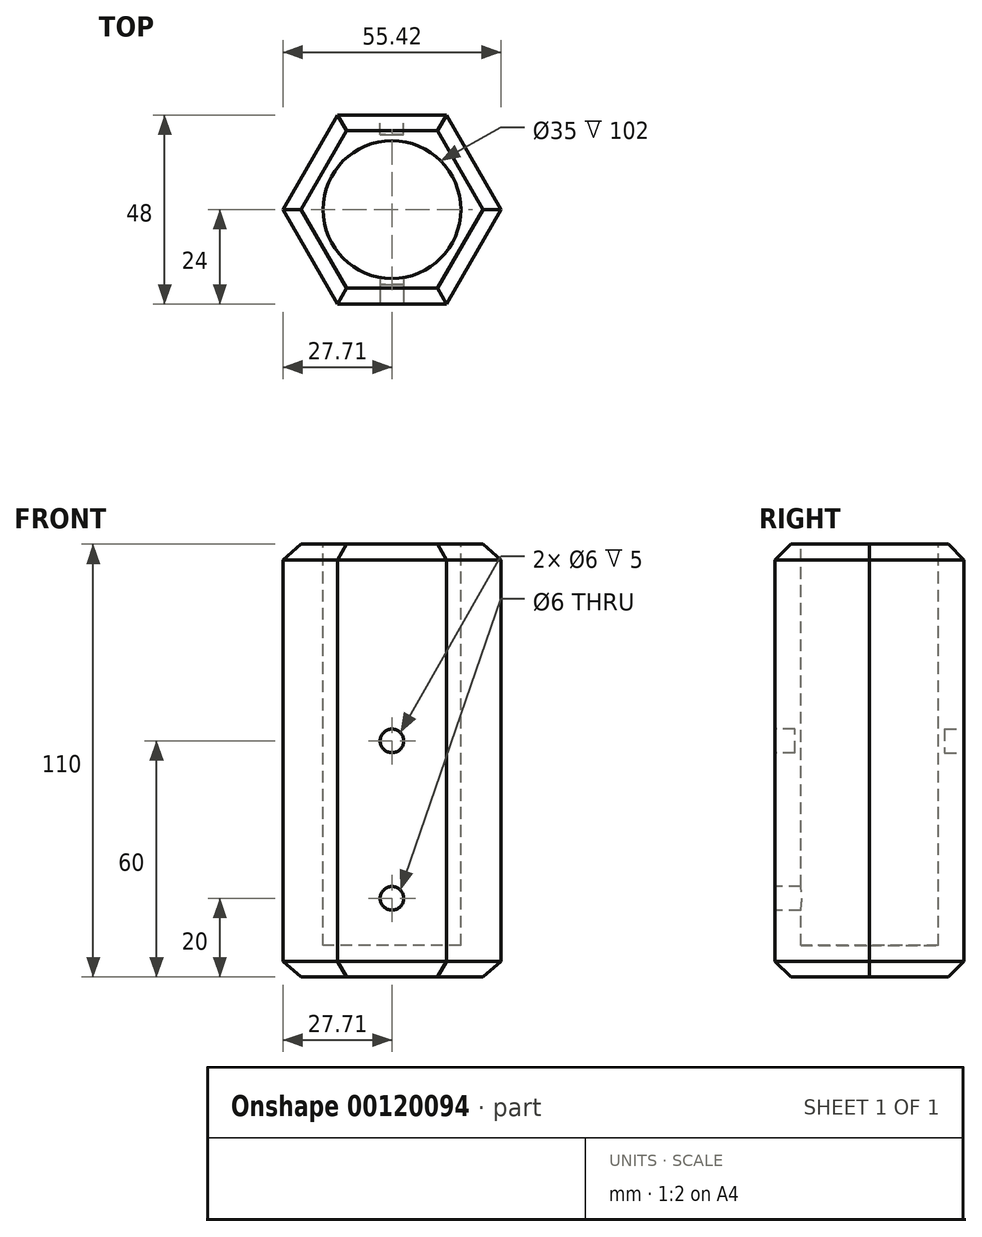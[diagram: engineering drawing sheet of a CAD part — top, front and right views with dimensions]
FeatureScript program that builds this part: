
annotation { "Feature Type Name" : "Feature", "Feature Type Description" : "" }
export const myFeature = defineFeature(function(context is Context, id is Id, definition is map)
    precondition{}
    {
        {
            var Q0;
            Q0=qCreatedBy(makeId("Top.planeOp"),FACE);
            var sketch = newSketch(context, id + "F0", { "sketchPlane" : qUnion([Q0])});
            skCircle(sketch, "E0.cCircle", {"center": v(0, 0) * mm, "radius": 24 * mm, "construction": true});
            skLineSegment(sketch, "E0.0", {"start": v(13.86, -24) * mm, "end": v(-13.86, -24) * mm});
            skLineSegment(sketch, "E0.1", {"start": v(-13.86, -24) * mm, "end": v(-27.71, 0) * mm});
            skLineSegment(sketch, "E0.2", {"start": v(-27.71, 0) * mm, "end": v(-13.86, 24) * mm});
            skLineSegment(sketch, "E0.3", {"start": v(-13.86, 24) * mm, "end": v(13.86, 24) * mm});
            skLineSegment(sketch, "E0.4", {"start": v(13.86, 24) * mm, "end": v(27.71, 0) * mm});
            skLineSegment(sketch, "E0.5", {"start": v(27.71, 0) * mm, "end": v(13.86, -24) * mm});
            skPoint(sketch, "E0.0.midPoint", {"position": v(0, -24) * mm});
            skSolve(sketch);
        }
        {
            var Q0;
            Q0 = qSketchRegion(id + "F0", true);
            extrude(context, id + "F1", {"entities" : qUnion([Q0]), "endBound" : BoundingType.SYMMETRIC, "depth" : 110 * mm});
        }
        {
            var Q0;
            Q0=makeQuery(id+"F1.opExtrude","CAP_FACE",FACE,{"disambiguationData":[OSD([sQuery(id+"F0.wireOp",EDGE,"E0.0"),sQuery(id+"F0.wireOp",EDGE,"E0.1"),sQuery(id+"F0.wireOp",EDGE,"E0.2"),sQuery(id+"F0.wireOp",EDGE,"E0.3"),sQuery(id+"F0.wireOp",EDGE,"E0.4"),sQuery(id+"F0.wireOp",EDGE,"E0.5")])],"isStart":false});
            var sketch = newSketch(context, id + "F2", { "sketchPlane" : qUnion([Q0])});
            skCircle(sketch, "E1", {"center": v(0, 0) * mm, "radius": 17.5 * mm});
            skSolve(sketch);
        }
        {
            var Q0;
            Q0 = qSketchRegion(id + "F2", true);
            extrude(context, id + "F3", {"entities" : qUnion([Q0]), "operationType" : NewBodyOperationType.REMOVE, "oppositeDirection" : true, "depth" : 102 * mm});
        }
        {
            var Q0;
            Q0=makeQuery(id+"F1.opExtrude","SWEPT_FACE",FACE,{"disambiguationData":[OSD([sQuery(id+"F0.wireOp",EDGE,"E0.0")])]});
            var sketch = newSketch(context, id + "F4", { "sketchPlane" : qUnion([Q0])});
            skLineSegment(sketch, "E2", {"start": v(0, -55) * mm, "end": v(0, 5) * mm});
            skPoint(sketch, "E2.endSnap0", {"position": v(0, -55) * mm});
            skCircle(sketch, "E3", {"center": v(0, 5) * mm, "radius": 3 * mm});
            skSolve(sketch);
        }
        {
            var Q0;
            Q0 = qSketchRegion(id + "F4", true);
            extrude(context, id + "F5", {"entities" : qUnion([Q0]), "operationType" : NewBodyOperationType.REMOVE, "oppositeDirection" : true, "depth" : 5 * mm});
        }
        {
            var Q0;
            Q0=makeQuery(id+"F1.opExtrude","SWEPT_FACE",FACE,{"disambiguationData":[OSD([sQuery(id+"F0.wireOp",EDGE,"E0.0")])]});
            var sketch = newSketch(context, id + "F6", { "sketchPlane" : qUnion([Q0])});
            skLineSegment(sketch, "E4", {"start": v(0, 5) * mm, "end": v(0, -35) * mm});
            skCircle(sketch, "E5", {"center": v(0, -35) * mm, "radius": 0.5 * mm});
            skCircle(sketch, "E6", {"center": v(0, -35) * mm, "radius": 3 * mm});
            skSolve(sketch);
        }
        {
            var Q0;
            Q0 = qSketchRegion(id + "F6", true);
            var Q1;
            Q1=makeQuery(id+"F6.imprint","IMPRINT",FACE,{"disambiguationData":[TD([[makeQuery(id+"F6.imprint","IMPRINT",EDGE,{"derivedFrom":sQuery(id+"F6.wireOp",EDGE,"E5")}),1.0]])]});
            extrude(context, id + "F7", {"entities" : qUnion([Q0, Q1]), "operationType" : NewBodyOperationType.REMOVE, "oppositeDirection" : true, "depth" : 25 * mm});
        }
        {
            var Q0;
            Q0=makeQuery(id+"F1.opExtrude","SWEPT_FACE",FACE,{"disambiguationData":[OSD([sQuery(id+"F0.wireOp",EDGE,"E0.3")])]});
            var sketch = newSketch(context, id + "F8", { "sketchPlane" : qUnion([Q0])});
            skLineSegment(sketch, "E7", {"start": v(0, -55) * mm, "end": v(0, 5) * mm});
            skCircle(sketch, "E8", {"center": v(0, 5) * mm, "radius": 3 * mm});
            skSolve(sketch);
        }
        {
            var Q0;
            Q0=makeQuery(id+"F8.imprint","IMPRINT",FACE,{"disambiguationData":[TD([[makeQuery(id+"F8.imprint","IMPRINT",EDGE,{"derivedFrom":sQuery(id+"F8.wireOp",EDGE,"E8")}),1.0]])]});
            extrude(context, id + "F9", {"entities" : qUnion([Q0]), "operationType" : NewBodyOperationType.REMOVE, "oppositeDirection" : true, "depth" : 5 * mm});
        }
        {
            var Q0;
            Q0=makeQuery(id+"F1.opExtrude","CAP_EDGE",EDGE,{"disambiguationData":[OSD([sQuery(id+"F0.wireOp",EDGE,"E0.1")])],"isStart":false});
            var Q1;
            Q1=makeQuery(id+"F1.opExtrude","CAP_EDGE",EDGE,{"disambiguationData":[OSD([sQuery(id+"F0.wireOp",EDGE,"E0.0")])],"isStart":false});
            var Q2;
            Q2=makeQuery(id+"F1.opExtrude","CAP_EDGE",EDGE,{"disambiguationData":[OSD([sQuery(id+"F0.wireOp",EDGE,"E0.3")])],"isStart":false});
            var Q3;
            Q3=makeQuery(id+"F1.opExtrude","CAP_EDGE",EDGE,{"disambiguationData":[OSD([sQuery(id+"F0.wireOp",EDGE,"E0.4")])],"isStart":false});
            var Q4;
            Q4=makeQuery(id+"F1.opExtrude","CAP_EDGE",EDGE,{"disambiguationData":[OSD([sQuery(id+"F0.wireOp",EDGE,"E0.5")])],"isStart":false});
            var Q5;
            Q5=makeQuery(id+"F1.opExtrude","CAP_EDGE",EDGE,{"disambiguationData":[OSD([sQuery(id+"F0.wireOp",EDGE,"E0.2")])],"isStart":false});
            var Q6;
            Q6=makeQuery(id+"F1.opExtrude","CAP_FACE",FACE,{"disambiguationData":[OSD([sQuery(id+"F0.wireOp",EDGE,"E0.0"),sQuery(id+"F0.wireOp",EDGE,"E0.1"),sQuery(id+"F0.wireOp",EDGE,"E0.2"),sQuery(id+"F0.wireOp",EDGE,"E0.3"),sQuery(id+"F0.wireOp",EDGE,"E0.4"),sQuery(id+"F0.wireOp",EDGE,"E0.5")])],"isStart":true});
            chamfer(context, id + "F10", {"entities" : qUnion([Q0, Q1, Q2, Q3, Q4, Q5, Q6]), "width" : 4 * mm, "tangentPropagation" : true});
        }
    });
